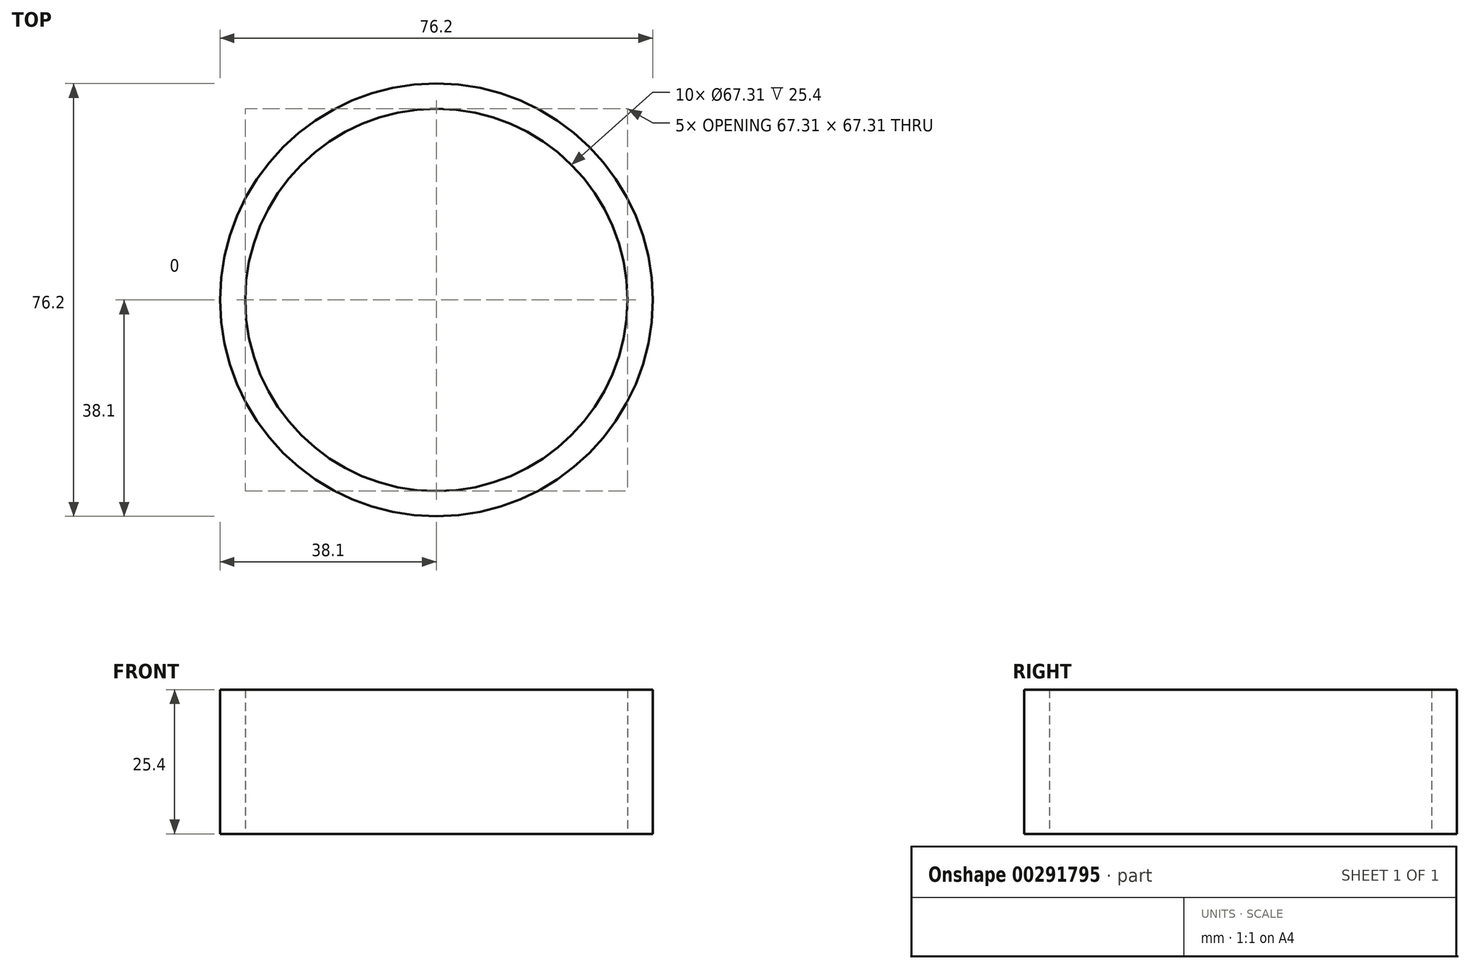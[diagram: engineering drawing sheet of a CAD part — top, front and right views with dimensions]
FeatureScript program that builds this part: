
annotation { "Feature Type Name" : "Feature", "Feature Type Description" : "" }
export const myFeature = defineFeature(function(context is Context, id is Id, definition is map)
    precondition{}
    {
        {
            var Q0;
            Q0=qCreatedBy(makeId("Top.planeOp"),FACE);
            var sketch = newSketch(context, id + "F0", { "sketchPlane" : qUnion([Q0])});
            skCircle(sketch, "E0", {"center": v(0, 0) * mm, "radius": 38.1 * mm});
            skSolve(sketch);
        }
        {
            var Q0;
            Q0 = qSketchRegion(id + "F0", true);
            extrude(context, id + "F1", {"entities" : qUnion([Q0]), "depth" : 25.4 * mm});
        }
        {
            var Q0;
            Q0=sQuery(id+"F0.wireOp",VERTEX,"E0.center");
            var Q1;
            Q1=makeQuery(id+"F1.opExtrude","SWEPT_BODY",BODY,{"disambiguationData":[OSD([sQuery(id+"F0.wireOp",EDGE,"E0")])]});
            hole(context, id + "F2", {"style" : HoleStyle.SIMPLE, "endStyle" : HoleEndStyle.THROUGH, "oppositeDirection" : true, "holeDiameter" : 67.3 * mm, "tappedDepth" : 12.7 * mm, "tapClearance" : 3, "locations" : qUnion([Q0]), "scope" : qUnion([Q1])});
        }
    });
